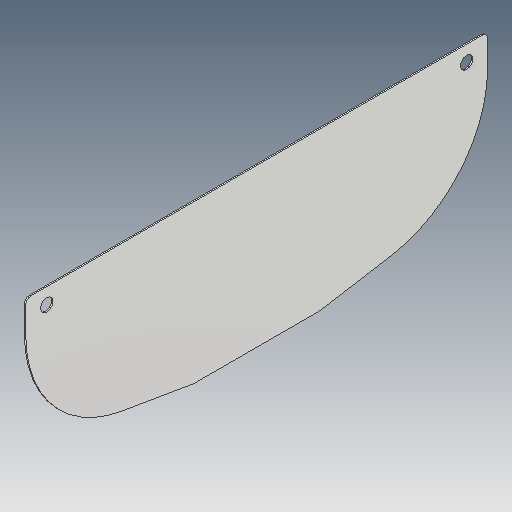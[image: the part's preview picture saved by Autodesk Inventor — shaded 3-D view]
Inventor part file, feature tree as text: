
AUTODESK INVENTOR PART (.ipt)
format: ipt  version: 2023.5 (Build 275446000, 446)  size: 92,160 bytes
history: native  units: in
note: dims shown in document units (in); Inventor stores cm internally (conversion verified against a paired STEP export)
features: fillet x1
ambient origin geometry x8: Origin, YZ Plane, XZ Plane, XY Plane, X Axis, Y Axis, Z Axis, Center Point
bodies: Solid1 (feature_tree)
feature tree (1):
  fillet  "Fillet1"  [1 undecoded]
note: 1 required parameter value undecoded (feature->parameter linkage not recoverable at this tier; creation-order binding heuristic only, values carry confidence <= 0.55)
